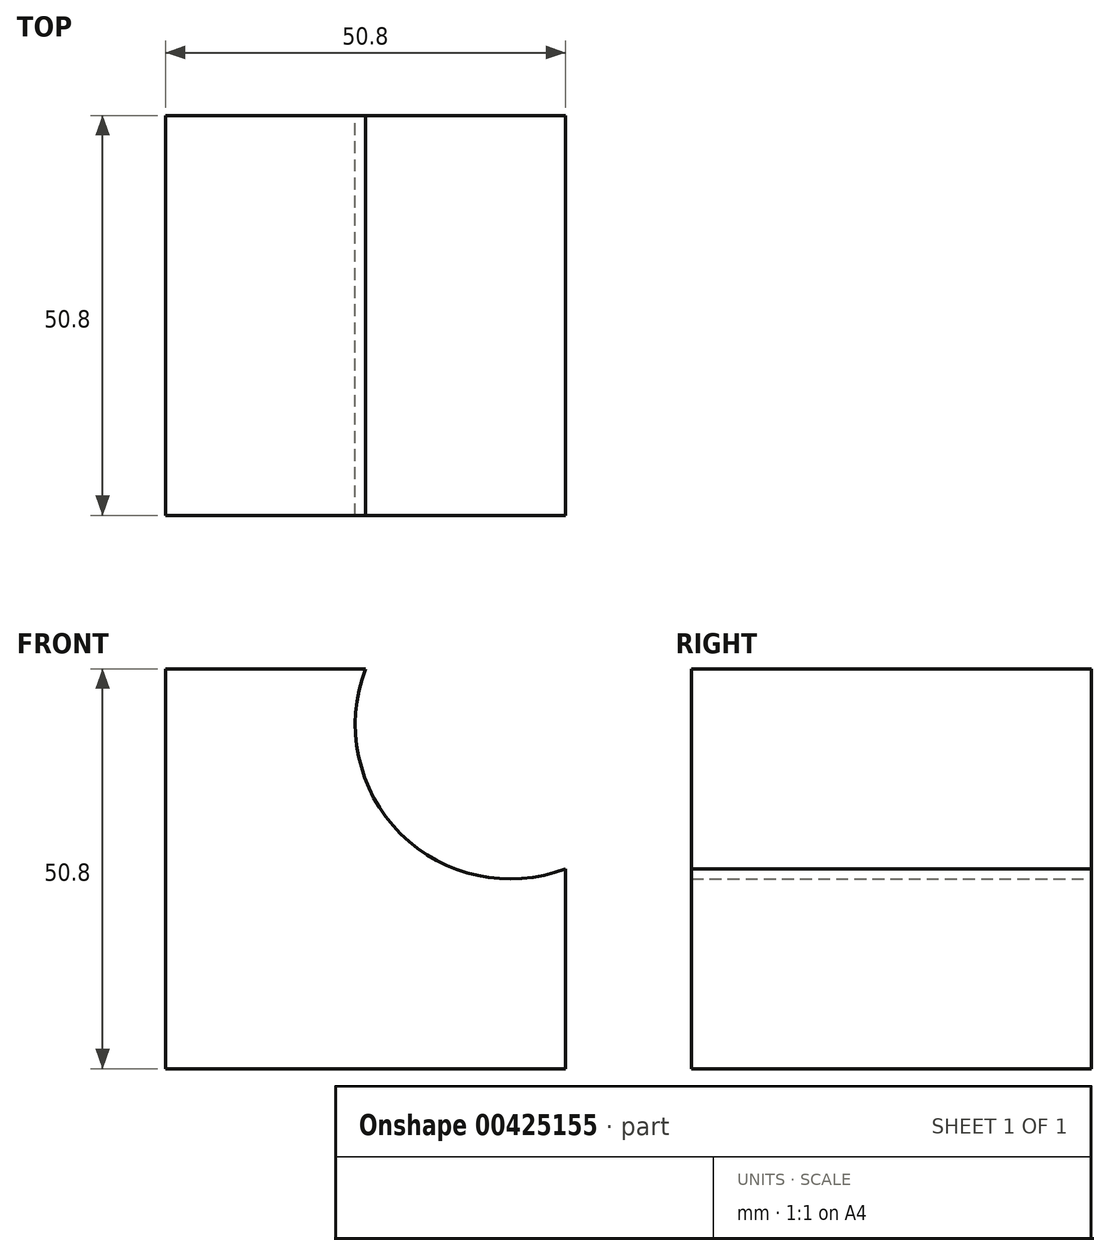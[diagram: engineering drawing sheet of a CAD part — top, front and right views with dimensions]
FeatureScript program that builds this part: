
annotation { "Feature Type Name" : "Feature", "Feature Type Description" : "" }
export const myFeature = defineFeature(function(context is Context, id is Id, definition is map)
    precondition{}
    {
        {
            var Q0;
            Q0=qCreatedBy(makeId("Front.planeOp"),FACE);
            var sketch = newSketch(context, id + "F0", { "sketchPlane" : qUnion([Q0])});
            skLineSegment(sketch, "E0", {"start": v(0, 0) * mm, "end": v(50.8, 0) * mm});
            skLineSegment(sketch, "E1", {"start": v(0, 0) * mm, "end": v(0, 50.8) * mm});
            skLineSegment(sketch, "E2", {"start": v(0, 50.8) * mm, "end": v(25.4, 50.8) * mm});
            skLineSegment(sketch, "E3", {"start": v(50.8, 0) * mm, "end": v(50.8, 25.4) * mm});
            skArc(sketch, "E4", {"start": v(25.4, 50.8) * mm, "mid": v(29.85, 29.85) * mm, "end": v(50.8, 25.4) * mm});
            skSolve(sketch);
        }
        {
            var Q0;
            Q0 = qSketchRegion(id + "F0", true);
            extrude(context, id + "F1", {"entities" : qUnion([Q0]), "depth" : 50.8 * mm});
        }
    });
